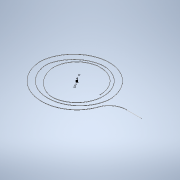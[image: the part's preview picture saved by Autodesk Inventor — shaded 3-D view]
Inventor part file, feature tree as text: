
AUTODESK INVENTOR PART (.ipt)
format: ipt  version: 2022.1 (Build 261234000, 234)  size: 349,696 bytes
history: native  units: mm
features: sketch x2, extrude x2, sweep x1
ambient origin geometry x8: Origin, YZ Plane, XZ Plane, XY Plane, X Axis, Y Axis, Z Axis, Center Point
bodies: Solid1 (feature_tree), Solid2 (feature_tree)
feature tree (5):
  sketch  "Sketch1"  dims[d0=150.0mm d1=165.0mm]
  sketch  "Sketch2"  dims[d2=180.0mm d3=135.0mm d4=75.0mm d5=120.0mm d6=93.167702mm d7=83.850932mm d8=74.534161mm d9=1.0mm d10=45.0mm d11=10.0mm d12=0.0mm d13=164.0mm d14=0.0mm d15=0.0mm d16=0.0mm d17=45.0mm]
  extrude  "Extrusion1"  Depth=165.0mm
  extrude  "Extrusion2"  Depth=74.534161mm
  sweep  "Sweep1"
